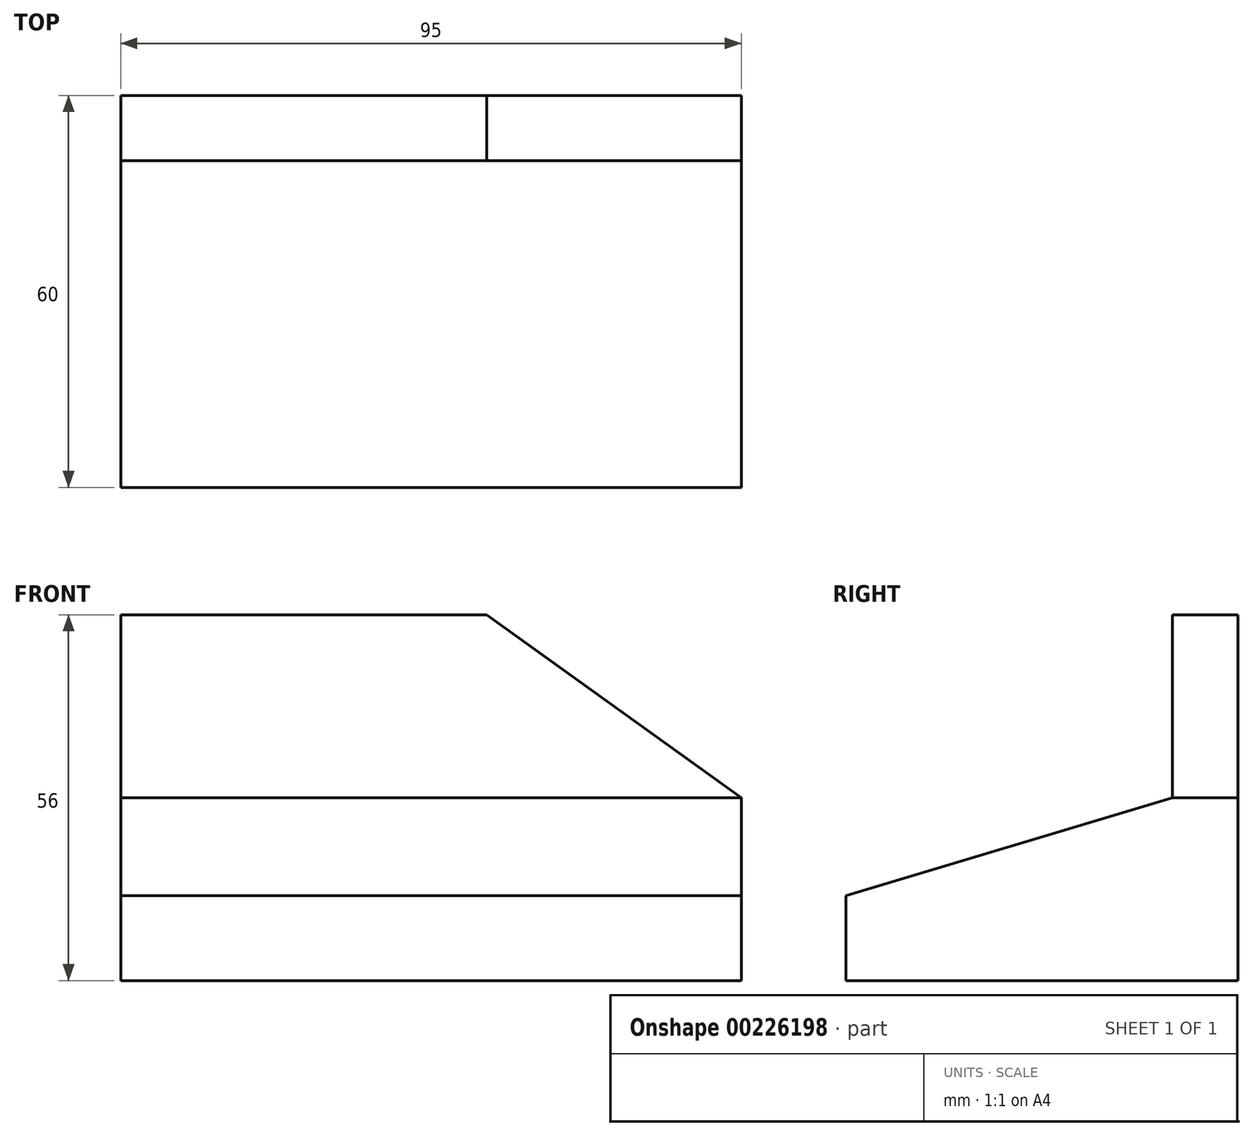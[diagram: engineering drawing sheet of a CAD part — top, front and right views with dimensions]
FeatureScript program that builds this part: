
annotation { "Feature Type Name" : "Feature", "Feature Type Description" : "" }
export const myFeature = defineFeature(function(context is Context, id is Id, definition is map)
    precondition{}
    {
        {
            var Q0;
            Q0=qCreatedBy(makeId("Right.planeOp"),FACE);
            var sketch = newSketch(context, id + "F0", { "sketchPlane" : qUnion([Q0])});
            skLineSegment(sketch, "E0", {"start": v(0, 0) * mm, "end": v(0, 56) * mm});
            skLineSegment(sketch, "E1", {"start": v(0, 56) * mm, "end": v(-10, 56) * mm});
            skLineSegment(sketch, "E2", {"start": v(-10, 56) * mm, "end": v(-10, 28) * mm});
            skLineSegment(sketch, "E3", {"start": v(-10, 28) * mm, "end": v(-60, 13) * mm});
            skLineSegment(sketch, "E4", {"start": v(-60, 13) * mm, "end": v(-60, 0) * mm});
            skLineSegment(sketch, "E5", {"start": v(-60, 0) * mm, "end": v(0, 0) * mm});
            skPoint(sketch, "E6", {"position": v(0, 28) * mm});
            skSolve(sketch);
        }
        {
            var Q0;
            Q0 = qSketchRegion(id + "F0", true);
            extrude(context, id + "F1", {"entities" : qUnion([Q0]), "depth" : 95 * mm});
        }
        {
            var Q0;
            Q0=makeQuery(id+"F1.opExtrude","SWEPT_FACE",FACE,{"disambiguationData":[OSD([sQuery(id+"F0.wireOp",EDGE,"E2")])]});
            var sketch = newSketch(context, id + "F2", { "sketchPlane" : qUnion([Q0])});
            skLineSegment(sketch, "E7", {"start": v(56, 56) * mm, "end": v(95, 28) * mm});
            skSolve(sketch);
        }
        {
            var Q0;
            Q0 = qSketchRegion(id + "F2", true);
            var Q1;
            {var subQ0=sQuery(id+"F2.wireOp",EDGE,"E7");Q1=makeQuery(id+"F2.imprint","IMPRINT",FACE,{"disambiguationData":[TD([[makeQuery(id+"F2.imprint","IMPRINT",EDGE,{"derivedFrom":subQ0}),1.0]])]});}
            extrude(context, id + "F3", {"entities" : qUnion([Q0, Q1]), "operationType" : NewBodyOperationType.REMOVE, "oppositeDirection" : true, "depth" : 25 * mm});
        }
    });
